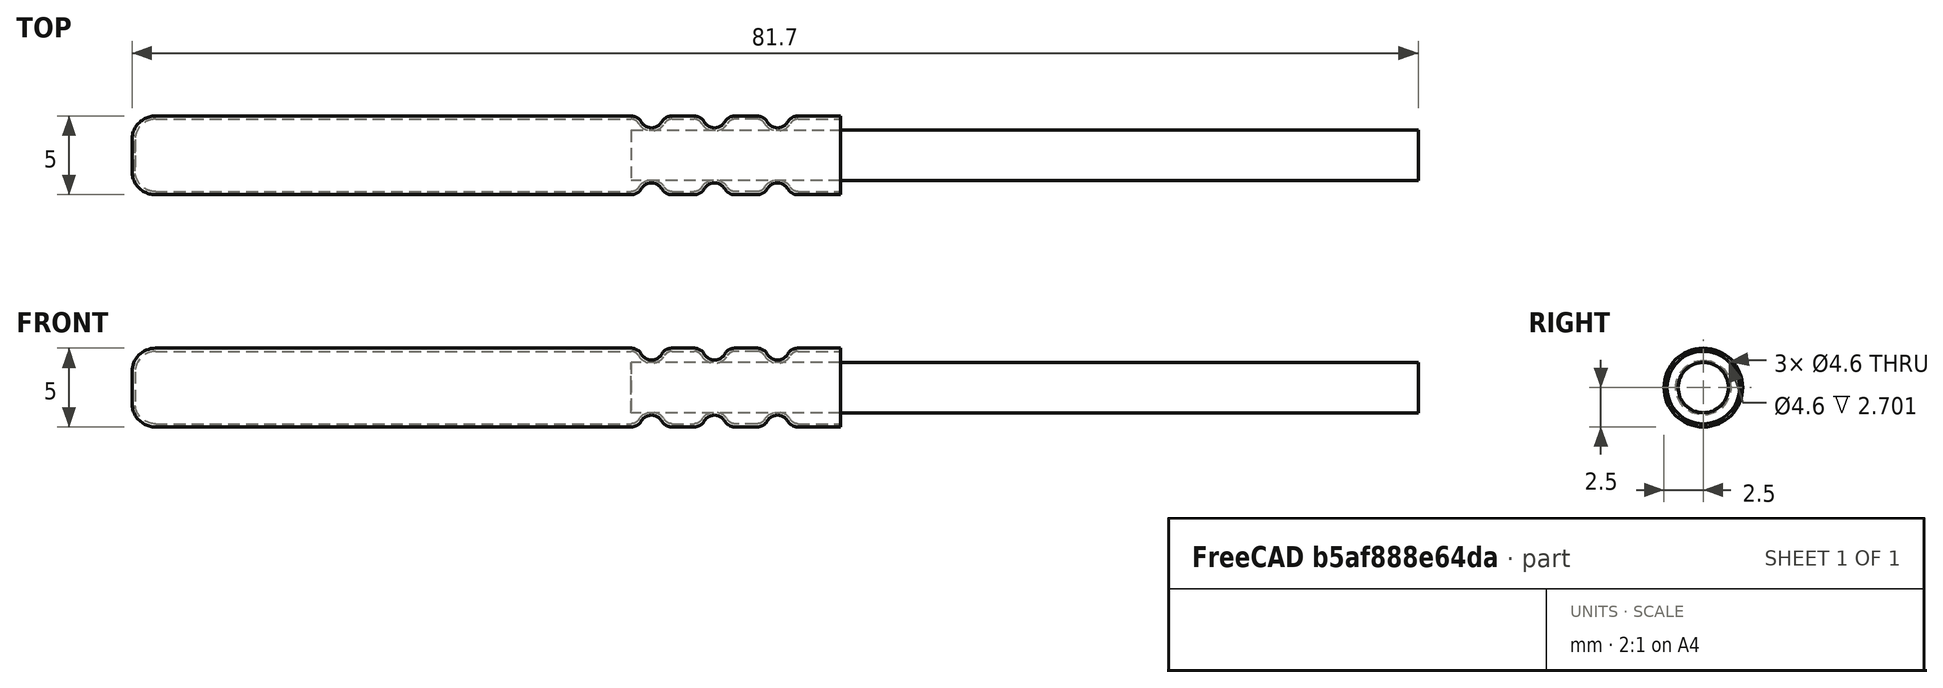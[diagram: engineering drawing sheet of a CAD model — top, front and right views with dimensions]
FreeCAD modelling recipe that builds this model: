
FCSTD DOCUMENT  (FreeCAD 0.20R26858 (Git))
Label: DigiTemp-Sens-OWire
License: All rights reserved
LicenseURL: http://en.wikipedia.org/wiki/All_rights_reserved
objects: TechDraw::DrawViewDimension×6, Sketcher::SketchObject×2, PartDesign::Body×2, App::VRMLObject×1, PartDesign::Revolution×1, PartDesign::Pad×1, TechDraw::DrawSVGTemplate×1, TechDraw::DrawProjGroupItem×1, TechDraw::DrawProjGroup×1, TechDraw::DrawPage×1
note: 8 computed .brp shape members not serialized (recipe doc carries the construction recipe); baked Part::Feature solids carry a one-line shape summary decoded from their .brp

FEATURE [App::VRMLObject] Digi_Temp_Sens_OWire  label="Digi-Temp-Sens-OWire"
  Placement = pos=(0,-2,-0.2) rot=(0,0,1;0rad)
  Resources = Digi_Temp_Sens_OWire/shapes3D/C_0603_1608Metric.wrl | Digi_Temp_Sens_OWire/shapes3D/MSOP-8_3x3mm_P0.65mm.wrl
FEATURE [Sketcher::SketchObject] Sketch
  FullyConstrained = true
  MapMode = 5
  Placement = pos=(0,0,0) rot=(1,0,0;1.5708rad)
  Support = -> [XZ_Plane]
  sketch-geometry (43):
    g0: LineSegment StartX=-11.7 StartY=0 StartZ=0 EndX=-11.7 EndY=1 EndZ=0
    g1: LineSegment StartX=-10.2 StartY=2.5 StartZ=0 EndX=20.001 EndY=2.5 EndZ=0
    g2: ArcOfCircle CenterX=-10.2 CenterY=1 CenterZ=0 NormalX=0 NormalY=0 NormalZ=1 AngleXU=0 Radius=1.5 StartAngle=1.5708 EndAngle=3.14159
    g3: LineSegment StartX=-11.7 StartY=0 StartZ=0 EndX=-11.5 EndY=0 EndZ=0
    g4: LineSegment StartX=-11.5 StartY=0 StartZ=0 EndX=-11.5 EndY=1 EndZ=0
    g5: ArcOfCircle CenterX=-10.2 CenterY=1 CenterZ=0 NormalX=0 NormalY=0 NormalZ=1 AngleXU=0 Radius=1.3 StartAngle=1.5708 EndAngle=3.14159
    g6: LineSegment StartX=-10.2 StartY=2.3 StartZ=0 EndX=20.001 EndY=2.3 EndZ=0
    g7: ArcOfCircle CenterX=20.001 CenterY=1.75 CenterZ=0 NormalX=0 NormalY=0 NormalZ=1 AngleXU=0 Radius=0.75 StartAngle=0.523599 EndAngle=1.5708
    g8: ArcOfCircle CenterX=21.3 CenterY=2.5 CenterZ=0 NormalX=0 NormalY=0 NormalZ=1 AngleXU=0 Radius=0.75 StartAngle=3.66519 EndAngle=5.75959
    g9: ArcOfCircle CenterX=22.599 CenterY=1.75 CenterZ=0 NormalX=0 NormalY=0 NormalZ=1 AngleXU=0 Radius=0.75 StartAngle=1.5708 EndAngle=2.61799
    g10: GeomPoint X=21.3 Y=1.75 Z=0
    g11: LineSegment StartX=20.001 StartY=2.5 StartZ=0 EndX=22.599 EndY=2.5 EndZ=0
    g12: LineSegment StartX=21.3 StartY=2.5 StartZ=0 EndX=21.3 EndY=0 EndZ=0
    g13: ArcOfCircle CenterX=24.001 CenterY=1.75 CenterZ=0 NormalX=0 NormalY=0 NormalZ=1 AngleXU=0 Radius=0.75 StartAngle=0.523599 EndAngle=1.5708
    g14: ArcOfCircle CenterX=25.3 CenterY=2.5 CenterZ=0 NormalX=0 NormalY=0 NormalZ=1 AngleXU=0 Radius=0.75 StartAngle=3.66519 EndAngle=5.75959
    g15: ArcOfCircle CenterX=26.599 CenterY=1.75 CenterZ=0 NormalX=0 NormalY=0 NormalZ=1 AngleXU=0 Radius=0.75 StartAngle=1.5708 EndAngle=2.61799
    g16: GeomPoint X=25.3 Y=1.75 Z=0
    g17: LineSegment StartX=24.001 StartY=2.5 StartZ=0 EndX=26.599 EndY=2.5 EndZ=0
    g18: ArcOfCircle CenterX=28.001 CenterY=1.75 CenterZ=0 NormalX=0 NormalY=0 NormalZ=1 AngleXU=0 Radius=0.75 StartAngle=0.523599 EndAngle=1.5708
    g19: ArcOfCircle CenterX=29.3 CenterY=2.5 CenterZ=0 NormalX=0 NormalY=0 NormalZ=1 AngleXU=0 Radius=0.75 StartAngle=3.66519 EndAngle=5.75959
    g20: ArcOfCircle CenterX=30.599 CenterY=1.75 CenterZ=0 NormalX=0 NormalY=0 NormalZ=1 AngleXU=0 Radius=0.75 StartAngle=1.5708 EndAngle=2.61799
    g21: GeomPoint X=29.3 Y=1.75 Z=0
    g22: LineSegment StartX=28.001 StartY=2.5 StartZ=0 EndX=30.599 EndY=2.5 EndZ=0
    g23: LineSegment StartX=25.3 StartY=2.5 StartZ=0 EndX=25.3 EndY=0 EndZ=0
    g24: LineSegment StartX=29.3 StartY=2.5 StartZ=0 EndX=29.3 EndY=0 EndZ=0
    g25: LineSegment StartX=21.3 StartY=1.75 StartZ=0 EndX=25.3 EndY=1.75 EndZ=0
    g26: LineSegment StartX=25.3 StartY=1.75 StartZ=0 EndX=29.3 EndY=1.75 EndZ=0
    g27: LineSegment StartX=22.599 StartY=2.5 StartZ=0 EndX=24.001 EndY=2.5 EndZ=0
    g28: LineSegment StartX=26.599 StartY=2.5 StartZ=0 EndX=28.001 EndY=2.5 EndZ=0
    g29: LineSegment StartX=30.599 StartY=2.5 StartZ=0 EndX=33.3 EndY=2.5 EndZ=0
    g30: LineSegment StartX=33.3 StartY=2.5 StartZ=0 EndX=33.3 EndY=2.3 EndZ=0
    g31: ArcOfCircle CenterX=20.001 CenterY=1.75 CenterZ=0 NormalX=0 NormalY=0 NormalZ=1 AngleXU=0 Radius=0.55 StartAngle=0.523599 EndAngle=1.5708
    g32: ArcOfCircle CenterX=21.3 CenterY=2.5 CenterZ=0 NormalX=0 NormalY=0 NormalZ=1 AngleXU=0 Radius=0.95 StartAngle=3.66519 EndAngle=5.75959
    g33: ArcOfCircle CenterX=22.599 CenterY=1.75 CenterZ=0 NormalX=0 NormalY=0 NormalZ=1 AngleXU=0 Radius=0.55 StartAngle=1.5708 EndAngle=2.61799
    g34: ArcOfCircle CenterX=24.001 CenterY=1.75 CenterZ=0 NormalX=0 NormalY=0 NormalZ=1 AngleXU=0 Radius=0.55 StartAngle=0.523599 EndAngle=1.5708
    g35: ArcOfCircle CenterX=25.3 CenterY=2.5 CenterZ=0 NormalX=0 NormalY=0 NormalZ=1 AngleXU=0 Radius=0.95 StartAngle=3.66519 EndAngle=5.75959
    g36: ArcOfCircle CenterX=26.599 CenterY=1.75 CenterZ=0 NormalX=0 NormalY=0 NormalZ=1 AngleXU=0 Radius=0.55 StartAngle=1.5708 EndAngle=2.61799
    g37: ArcOfCircle CenterX=28.001 CenterY=1.75 CenterZ=0 NormalX=0 NormalY=0 NormalZ=1 AngleXU=0 Radius=0.55 StartAngle=0.523599 EndAngle=1.5708
    g38: ArcOfCircle CenterX=29.3 CenterY=2.5 CenterZ=0 NormalX=0 NormalY=0 NormalZ=1 AngleXU=0 Radius=0.95 StartAngle=3.66519 EndAngle=5.75959
    g39: ArcOfCircle CenterX=30.599 CenterY=1.75 CenterZ=0 NormalX=0 NormalY=0 NormalZ=1 AngleXU=0 Radius=0.55 StartAngle=1.5708 EndAngle=2.61799
    g40: LineSegment StartX=28.001 StartY=2.3 StartZ=0 EndX=26.599 EndY=2.3 EndZ=0
    g41: LineSegment StartX=30.599 StartY=2.3 StartZ=0 EndX=33.3 EndY=2.3 EndZ=0
    g42: LineSegment StartX=22.599 StartY=2.3 StartZ=0 EndX=24.001 EndY=2.3 EndZ=0
  constraints (108):
    c: PointOnObject(g0,g-1)
    c: Horizontal(g1)
    c: Tangent(g1,g2) = 1.5708
    c: Tangent(g0,g2) = 1.5708
    c: Vertical(g0)
    c: Radius(g2) = 1.5
    c: Coincident(g3,g0)
    c: Horizontal(g3)
    c: Coincident(g4,g3)
    c: Vertical(g4)
    c: Distance(g3) = 0.2
    c: Coincident(g5,g2)
    c: Tangent(g5,g4) = 1.5708
    c: Horizontal(g6)
    c: Tangent(g5,g6) = 1.5708
    c: DistanceY(g-1,g1) = 2.5
    c: Distance(g-1,g3) = 11.5
    c: Tangent(g7,g1) = 1.5708
    c: Tangent(g7,g8) = 1.5708
    c: Tangent(g8,g9) = 1.5708
    c: PointOnObject(g10,g8)
    c: Coincident(g11,g1)
    c: Coincident(g11,g9)
    c: Tangent(g11,g9)
    c: PointOnObject(g8,g11)
    c: Horizontal(g11)
    c: Coincident(g12,g8)
    c: PointOnObject(g12,g-1)
    c: Vertical(g12)
    c: PointOnObject(g10,g12)
    c: Tangent(g13,g14) = 1.5708
    c: Tangent(g14,g15) = 1.5708
    c: PointOnObject(g16,g14)
    c: Equal(g8,g14) = 1
    c: Coincident(g17,g15)
    c: Tangent(g17,g15)
    c: PointOnObject(g14,g17)
    c: Horizontal(g17)
    c: Tangent(g18,g19) = 1.5708
    c: Tangent(g19,g20) = 1.5708
    c: PointOnObject(g21,g19)
    c: Coincident(g22,g20)
    c: Tangent(g22,g20)
    c: PointOnObject(g19,g22)
    c: Horizontal(g22)
    c: Coincident(g23,g14)
    c: PointOnObject(g23,g-1)
    c: Vertical(g23)
    c: Coincident(g24,g19)
    c: PointOnObject(g24,g-1)
    c: Vertical(g24)
    c: PointOnObject(g21,g24)
    c: PointOnObject(g16,g23)
    c: Coincident(g25,g10)
    c: Coincident(g25,g16)
    c: Horizontal(g25)
    c: Coincident(g26,g16)
    c: Coincident(g26,g21)
    c: Horizontal(g26)
    c: Equal(g26,g25)
    c: DistanceX(g25,g25) = 4
    c: Coincident(g13,g17)
    c: Coincident(g18,g22)
    c: Coincident(g27,g9)
    c: Coincident(g27,g13)
    c: Coincident(g28,g15)
    c: Coincident(g28,g18)
    c: Horizontal(g28)
    c: Equal(g9,g7)
    c: Equal(g9,g13)
    c: Equal(g13,g15)
    c: Equal(g15,g18)
    c: Equal(g18,g20)
    c: Tangent(g13,g27,g13) = 1.5708
    c: Tangent(g18,g28,g18) = 1.5708
    c: Coincident(g29,g20)
    c: Horizontal(g29)
    c: Coincident(g30,g29)
    c: Vertical(g30)
    c: DistanceX(g0,g29) = 45
    c: Coincident(g31,g7)
    c: Coincident(g32,g8)
    c: Coincident(g33,g9)
    c: Tangent(g6,g31) = 1.5708
    c: Tangent(g31,g32) = 1.5708
    c: Tangent(g33,g32) = 1.5708
    c: Coincident(g34,g13)
    c: Coincident(g35,g14)
    c: Coincident(g36,g15)
    c: Coincident(g37,g18)
    c: Coincident(g38,g19)
    c: Coincident(g39,g20)
    c: Horizontal(g40)
    c: Horizontal(g41)
    c: Coincident(g30,g41)
    c: Tangent(g39,g41) = 1.5708
    c: Tangent(g39,g38) = 1.5708
    c: Tangent(g38,g37) = 1.5708
    c: Tangent(g37,g40) = -1.5708
    c: Tangent(g36,g40) = -1.5708
    c: Tangent(g35,g36) = 1.5708
    c: Tangent(g35,g34) = 1.5708
    c: Horizontal(g42)
    c: Tangent(g33,g42) = 1.5708
    c: Tangent(g42,g34) = 1.5708
    c: DistanceX(g19,g29) = 4
    c: Equal(g8,g7)
    c: DistanceY(g12,g10) = 1.75
FEATURE [PartDesign::Revolution] Revolution
  Angle = 360
  Axis = (1,0,0)
  Base = (0,0,0)
  Placement = pos=(0,0,0) rot=(1,0,0;1.5708rad)
  Profile = -> Sketch
  ReferenceAxis = -> X_Axis
FEATURE [PartDesign::Body] Body  label="Huelse"
  Group = -> [Sketch,Revolution]
  Origin = -> Origin
  Tip = -> Revolution
FEATURE [Sketcher::SketchObject] Sketch001
  AttachmentOffset = pos=(0,0,20) rot=(0,0,1;0rad)
  FullyConstrained = true
  MapMode = 5
  Placement = pos=(20,-4.4e-15,4.4e-15) rot=(0.57735,0.57735,0.57735;2.0944rad)
  Support = -> [YZ_Plane001]
  sketch-geometry (1):
    g0: Circle CenterX=0 CenterY=0 CenterZ=0 NormalX=0 NormalY=0 NormalZ=1 AngleXU=0 Radius=1.6
  constraints (2):
    c: Coincident(g0,g-1)
    c: Diameter(g0) = 3.2
FEATURE [PartDesign::Pad] Pad
  Direction = (1,-2e-16,3e-16)
  Length = 50
  Length2 = 100
  Placement = pos=(0,0,0) rot=(0.57735,0.57735,0.57735;2.0944rad)
  Profile = -> Sketch001
  ReferenceAxis = -> Sketch001 [N_Axis]
  Type = 0
FEATURE [PartDesign::Body] Body001  label="Kabel"
  Group = -> [Sketch001,Pad]
  Origin = -> Origin001
  Tip = -> Pad
FEATURE [TechDraw::DrawSVGTemplate] Template
  EditableTexts = Designed_by_Name=Daniel Glaser; Drawing_number=20221111001; FC-Date=2022-11-11; FC-SC=2.5:1; FC-SH=1/1; FC-Title=Owire Temperatursensor; Subtitle=Typ PS 5x45mm; Weight=~2g
  Height = 210
  Orientation = 1
  Width = 297
FEATURE [TechDraw::DrawProjGroupItem] ProjItem  label="Front"
  CoarseView = false
  Direction = (0,-1,0)
  Focus = 100
  HardHidden = false
  IsoCount = 0
  IsoHidden = false
  IsoVisible = false
  LockPosition = true
  Perspective = false
  Rotation = 0
  RotationVector = (1,0,0)
  Scale = 2.5
  ScaleType = 2
  SeamHidden = false
  SeamVisible = true
  SmoothHidden = false
  SmoothVisible = true
  Source = -> [Body,Body001]
  Type = 0
  X = 0
  XDirection = (1,0,0)
  Y = 0
FEATURE [TechDraw::DrawProjGroup] ProjGroup
  Anchor = -> ProjItem
  AutoDistribute = true
  LockPosition = false
  ProjectionType = 0
  Rotation = 0
  Scale = 2.5
  ScaleType = 0
  Source = -> [Body,Body001]
  Views = -> [ProjItem]
  X = 155.419
  Y = 128.669
  spacingX = 20
  spacingY = 15
FEATURE [TechDraw::DrawViewDimension] Dimension004
  Arbitrary = false
  ArbitraryTolerances = false
  EqualTolerance = true
  FormatSpec = %.2f
  FormatSpecOverTolerance = %+.2f
  FormatSpecUnderTolerance = %+.2f
  Inverted = false
  LockPosition = false
  MeasureType = 1
  OverTolerance = 0
  References2D = -> [ProjItem]
  Rotation = 0
  ScaleType = 0
  TheoreticalExact = false
  Type = 2
  UnderTolerance = 0
  X = -112.361
  Y = 21.2591
FEATURE [TechDraw::DrawViewDimension] Dimension005
  Arbitrary = false
  ArbitraryTolerances = false
  EqualTolerance = true
  FormatSpec = %.2f
  FormatSpecOverTolerance = %+.2f
  FormatSpecUnderTolerance = %+.2f
  Inverted = false
  LockPosition = false
  MeasureType = 1
  OverTolerance = 0
  References2D = -> [ProjItem]
  Rotation = 0
  ScaleType = 0
  TheoreticalExact = false
  Type = 1
  UnderTolerance = 0
  X = -46.0282
  Y = -31.1871
FEATURE [TechDraw::DrawViewDimension] Dimension
  Arbitrary = false
  ArbitraryTolerances = false
  EqualTolerance = true
  FormatSpec = %.2f
  FormatSpecOverTolerance = %+.2f
  FormatSpecUnderTolerance = %+.2f
  Inverted = false
  LockPosition = false
  MeasureType = 1
  OverTolerance = 0
  References2D = -> [ProjItem]
  Rotation = 0
  ScaleType = 0
  TheoreticalExact = false
  Type = 2
  UnderTolerance = 0
  X = -32.3466
  Y = -20.2642
FEATURE [TechDraw::DrawViewDimension] Dimension009
  Arbitrary = false
  ArbitraryTolerances = false
  EqualTolerance = true
  FormatSpec = %.2f
  FormatSpecOverTolerance = %+.2f
  FormatSpecUnderTolerance = %+.2f
  Inverted = false
  LockPosition = false
  MeasureType = 1
  OverTolerance = 0
  References2D = -> [ProjItem]
  Rotation = 0
  ScaleType = 0
  TheoreticalExact = false
  Type = 1
  UnderTolerance = 0
  X = 21.0124
  Y = 18.0024
FEATURE [TechDraw::DrawViewDimension] Dimension010
  Arbitrary = false
  ArbitraryTolerances = false
  EqualTolerance = true
  FormatSpec = %.2f
  FormatSpecOverTolerance = %+.2f
  FormatSpecUnderTolerance = %+.2f
  Inverted = false
  LockPosition = false
  MeasureType = 1
  OverTolerance = 0
  References2D = -> [ProjItem]
  Rotation = 0
  ScaleType = 0
  TheoreticalExact = false
  Type = 1
  UnderTolerance = 0
  X = 8.48714
  Y = 27.4136
FEATURE [TechDraw::DrawViewDimension] Dimension011
  Arbitrary = false
  ArbitraryTolerances = false
  EqualTolerance = true
  FormatSpec = %.2f
  FormatSpecOverTolerance = %+.2f
  FormatSpecUnderTolerance = %+.2f
  Inverted = false
  LockPosition = false
  MeasureType = 1
  OverTolerance = 0
  References2D = -> [ProjItem]
  Rotation = 0
  ScaleType = 0
  TheoreticalExact = false
  Type = 1
  UnderTolerance = 0
  X = 8.24636
  Y = 35.9608
FEATURE [TechDraw::DrawPage] Page
  KeepUpdated = true
  NextBalloonIndex = 1
  ProjectionType = 0
  Template = -> Template
  Views = -> [ProjGroup,Dimension004,Dimension005,Dimension,Dimension009,Dimension010,Dimension011]
